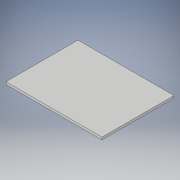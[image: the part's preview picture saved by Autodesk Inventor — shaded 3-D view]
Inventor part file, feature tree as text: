
AUTODESK INVENTOR PART (.ipt)
format: ipt  version: 2018 (Build 220112000, 112)  size: 89,600 bytes
history: native  units: in
note: dims shown in document units (in); Inventor stores cm internally (conversion verified against a paired STEP export)
features: extrude x1, sketch x1
ambient origin geometry x8: Origin, YZ Plane, XZ Plane, XY Plane, X Axis, Y Axis, Z Axis, Center Point
bodies: Solid1 (feature_tree)
feature tree (2):
  extrude  "Extrusion1"  Depth=3.0in
  sketch  "Sketch1"  dims[d0=4.0in d1=3.0in d2=0.1in d3=0.0in]
